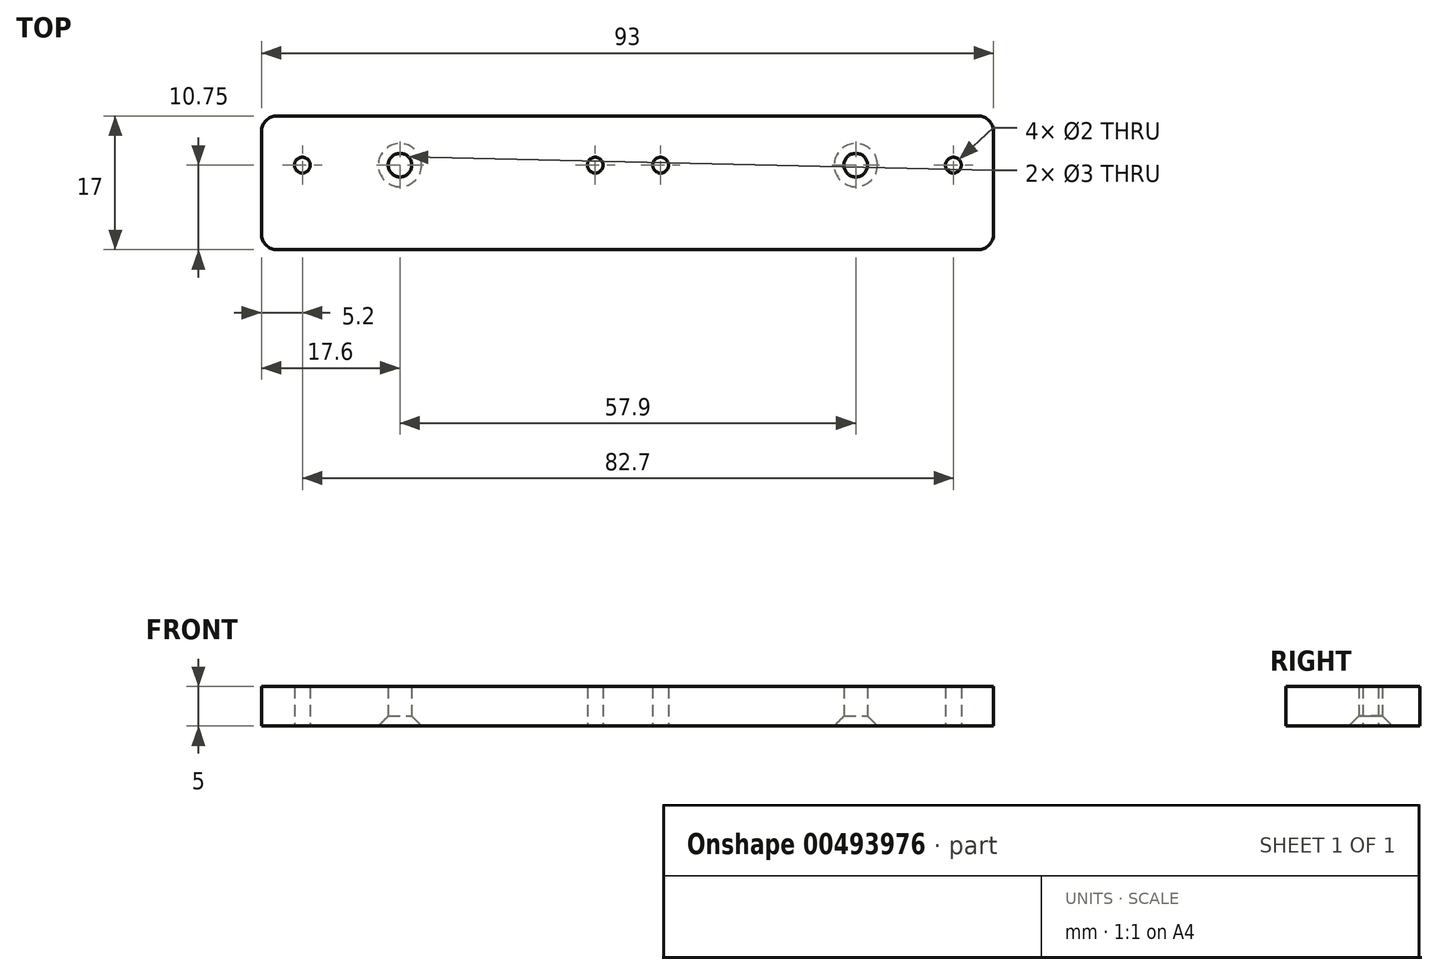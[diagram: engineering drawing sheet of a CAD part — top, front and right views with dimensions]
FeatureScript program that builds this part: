
annotation { "Feature Type Name" : "Feature", "Feature Type Description" : "" }
export const myFeature = defineFeature(function(context is Context, id is Id, definition is map)
    precondition{}
    {
        {
            var Q0;
            Q0=qCreatedBy(makeId("Top.planeOp"),FACE);
            var sketch = newSketch(context, id + "F0", { "sketchPlane" : qUnion([Q0])});
            skLineSegment(sketch, "E0.bottom", {"start": v(-46.5, 8.5) * mm, "end": v(46.5, 8.5) * mm});
            skLineSegment(sketch, "E0.top", {"start": v(-46.5, -8.5) * mm, "end": v(46.5, -8.5) * mm});
            skLineSegment(sketch, "E0.left", {"start": v(-46.5, 8.5) * mm, "end": v(-46.5, -8.5) * mm});
            skLineSegment(sketch, "E0.right", {"start": v(46.5, 8.5) * mm, "end": v(46.5, -8.5) * mm});
            skPoint(sketch, "E0.middle", {"position": v(0, 0) * mm});
            skPoint(sketch, "E1", {"position": v(41.4, 2.25) * mm});
            skPoint(sketch, "E2", {"position": v(4.2, 2.25) * mm});
            skPoint(sketch, "E3", {"position": v(-4.1, 2.25) * mm});
            skPoint(sketch, "E4", {"position": v(-41.3, 2.25) * mm});
            skPoint(sketch, "E5", {"position": v(-28.9, 2.25) * mm});
            skPoint(sketch, "E6", {"position": v(29, 2.25) * mm});
            skSolve(sketch);
        }
        {
            var Q0;
            Q0=makeQuery(id+"F0.imprint","IMPRINT",FACE,{"disambiguationData":[TD([[makeQuery(id+"F0.imprint","IMPRINT",EDGE,{"derivedFrom":sQuery(id+"F0.wireOp",EDGE,"E0.bottom")}),-1.0]])]});
            extrude(context, id + "F1", {"entities" : qUnion([Q0]), "depth" : 5 * mm});
        }
        {
            var Q0;
            Q0=sQuery(id+"F0.wireOp",VERTEX,"E4");
            var Q1;
            Q1=sQuery(id+"F0.wireOp",VERTEX,"E3");
            var Q2;
            Q2=sQuery(id+"F0.wireOp",VERTEX,"E2");
            var Q3;
            Q3=sQuery(id+"F0.wireOp",VERTEX,"E1");
            var Q4;
            Q4=makeQuery(id+"F1.opExtrude","SWEPT_BODY",BODY,{"disambiguationData":[OSD([sQuery(id+"F0.wireOp",EDGE,"E0.bottom"),sQuery(id+"F0.wireOp",EDGE,"E0.top"),sQuery(id+"F0.wireOp",EDGE,"E0.left"),sQuery(id+"F0.wireOp",EDGE,"E0.right")])]});
            hole(context, id + "F2", {"style" : HoleStyle.SIMPLE, "endStyle" : HoleEndStyle.THROUGH, "oppositeDirection" : true, "holeDiameter" : 2 * mm, "isTappedThrough" : true, "tappedDepth" : 12 * mm, "tapClearance" : 3, "startFromSketch" : true, "locations" : qUnion([Q0, Q1, Q2, Q3]), "scope" : qUnion([Q4])});
        }
        {
            var Q0;
            Q0=sQuery(id+"F0.wireOp",VERTEX,"E6");
            var Q1;
            Q1=sQuery(id+"F0.wireOp",VERTEX,"E5");
            var Q2;
            Q2=makeQuery(id+"F1.opExtrude","SWEPT_BODY",BODY,{"disambiguationData":[OSD([sQuery(id+"F0.wireOp",EDGE,"E0.bottom"),sQuery(id+"F0.wireOp",EDGE,"E0.top"),sQuery(id+"F0.wireOp",EDGE,"E0.left"),sQuery(id+"F0.wireOp",EDGE,"E0.right")])]});
            hole(context, id + "F3", {"style" : HoleStyle.C_SINK, "endStyle" : HoleEndStyle.THROUGH, "oppositeDirection" : true, "holeDiameter" : 3 * mm, "cSinkDiameter" : 5.5 * mm, "cSinkAngle" : 90 * degree, "isTappedThrough" : true, "tappedDepth" : 12 * mm, "tapClearance" : 3, "startFromSketch" : true, "locations" : qUnion([Q0, Q1]), "scope" : qUnion([Q2])});
        }
        {
            var Q0;
            Q0=makeQuery(id+"F1.opExtrude","SWEPT_EDGE",EDGE,{"disambiguationData":[OSD([sQuery(id+"F0.wireOp",EDGE,"E0.bottom"),sQuery(id+"F0.wireOp",EDGE,"E0.right")])]});
            var Q1;
            Q1=makeQuery(id+"F1.opExtrude","SWEPT_EDGE",EDGE,{"disambiguationData":[OSD([sQuery(id+"F0.wireOp",EDGE,"E0.top"),sQuery(id+"F0.wireOp",EDGE,"E0.right")])]});
            var Q2;
            Q2=makeQuery(id+"F1.opExtrude","SWEPT_EDGE",EDGE,{"disambiguationData":[OSD([sQuery(id+"F0.wireOp",EDGE,"E0.bottom"),sQuery(id+"F0.wireOp",EDGE,"E0.left")])]});
            var Q3;
            Q3=makeQuery(id+"F1.opExtrude","SWEPT_EDGE",EDGE,{"disambiguationData":[OSD([sQuery(id+"F0.wireOp",EDGE,"E0.top"),sQuery(id+"F0.wireOp",EDGE,"E0.left")])]});
            fillet(context, id + "F4", {"entities" : qUnion([Q0, Q1, Q2, Q3]), "radius" : 2 * mm, "tangentPropagation" : true, "allowEdgeOverflow" : false});
        }
    });
